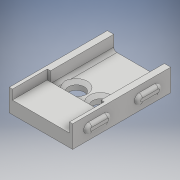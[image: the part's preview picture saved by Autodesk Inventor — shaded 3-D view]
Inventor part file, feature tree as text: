
AUTODESK INVENTOR PART (.ipt)
format: ipt  version: 2018 (Build 220112000, 112)  size: 229,376 bytes
history: native  units: mm
features: extrude x5, sketch x5, fillet x2, chamfer x1, plane x1, mirror x1, projected_geometry x1
ambient origin geometry x8: Origin, YZ Plane, XZ Plane, XY Plane, X Axis, Y Axis, Z Axis, Center Point
bodies: Solid1 (feature_tree)
feature tree (16):
  extrude  "Extrusion1"  Depth=31.0mm
  extrude  "Extrusion2"  Depth=20.0mm
  extrude  "Extrusion3"  Depth=2.0mm
  extrude  "Extrusion4"  Depth=1.0mm
  chamfer  "Chamfer1"  Distance=3.0mm
  extrude  "Extrusion5"  Depth=1.0mm
  plane  "Work Plane1"
  mirror  "Mirror1"
  fillet  "Fillet2"  Radius=5.0mm
  fillet  "Fillet3"  Radius=7.62mm
  sketch  "Sketch1"  dims[d0=20.0mm d1=31.0mm]
  sketch  "Sketch2"  dims[d2=7.0mm d3=0.0mm d4=20.0mm]
  sketch  "Sketch3"  dims[d5=2.0mm d6=2.0mm]
  sketch  "Sketch4"  dims[d7=4.5mm d8=0.0mm d9=1.0mm]
  projected_geometry  "Projected Loop1"
  sketch  "Sketch5"  dims[d10=1.0mm d11=3.0mm d12=0.0mm d13=5.0mm d14=5.0mm d15=7.62mm d16=15.0mm d17=90.0deg d18=3.0mm d19=0.0mm d20=1.0mm d21=2.0mm d22=45.0deg d23=31.0mm d24=90.0deg d25=3.0mm d26=3.0mm d27=5.0mm d28=5.0mm d29=5.0mm d30=5.0mm d31=1.0mm d32=0.0mm d34=1.0mm d35=1.0mm]
